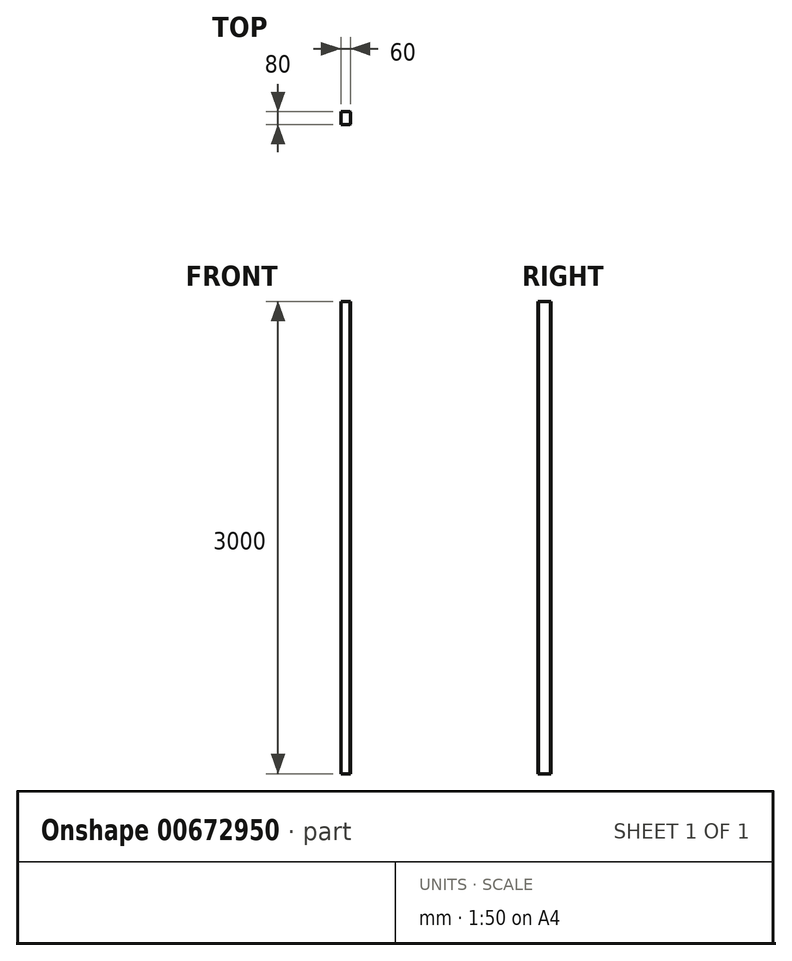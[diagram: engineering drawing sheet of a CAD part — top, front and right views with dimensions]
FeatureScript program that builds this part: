
annotation { "Feature Type Name" : "Feature", "Feature Type Description" : "" }
export const myFeature = defineFeature(function(context is Context, id is Id, definition is map)
    precondition{}
    {
        {
            var Q0;
            Q0=qCreatedBy(makeId("Top.planeOp"),FACE);
            var sketch = newSketch(context, id + "F0", { "sketchPlane" : qUnion([Q0])});
            skLineSegment(sketch, "E0.bottom", {"start": v(0, 0) * mm, "end": v(60, 0) * mm});
            skLineSegment(sketch, "E0.top", {"start": v(0, 80) * mm, "end": v(60, 80) * mm});
            skLineSegment(sketch, "E0.left", {"start": v(0, 0) * mm, "end": v(0, 80) * mm});
            skLineSegment(sketch, "E0.right", {"start": v(60, 0) * mm, "end": v(60, 80) * mm});
            skSolve(sketch);
        }
        {
            var Q0;
            Q0=makeQuery(id+"F0.imprint","IMPRINT",FACE,{"disambiguationData":[TD([[makeQuery(id+"F0.imprint","IMPRINT",EDGE,{"derivedFrom":sQuery(id+"F0.wireOp",EDGE,"E0.bottom")}),1.0]])]});
            extrude(context, id + "F1", {"entities" : qUnion([Q0]), "depth" : 3000 * mm, "offsetDistance" : 25 * mm});
        }
        {
            var Q0;
            Q0=makeQuery(id+"F1.opExtrude","SWEPT_EDGE",EDGE,{"disambiguationData":[OSD([sQuery(id+"F0.wireOp",EDGE,"E0.bottom"),sQuery(id+"F0.wireOp",EDGE,"E0.right")])]});
            chamfer(context, id + "F2", {"entities" : qUnion([Q0]), "width" : 1 * mm, "tangentPropagation" : true});
        }
        {
            var Q0;
            Q0=makeQuery(id+"F1.opExtrude","SWEPT_EDGE",EDGE,{"disambiguationData":[OSD([sQuery(id+"F0.wireOp",EDGE,"E0.bottom"),sQuery(id+"F0.wireOp",EDGE,"E0.left")])]});
            chamfer(context, id + "F3", {"entities" : qUnion([Q0]), "width" : 1 * mm, "tangentPropagation" : true});
        }
        {
            var Q0;
            Q0=makeQuery(id+"F1.opExtrude","SWEPT_EDGE",EDGE,{"disambiguationData":[OSD([sQuery(id+"F0.wireOp",EDGE,"E0.top"),sQuery(id+"F0.wireOp",EDGE,"E0.right")])]});
            chamfer(context, id + "F4", {"entities" : qUnion([Q0]), "width" : 1 * mm, "tangentPropagation" : true});
        }
        {
            var Q0;
            Q0=makeQuery(id+"F1.opExtrude","SWEPT_EDGE",EDGE,{"disambiguationData":[OSD([sQuery(id+"F0.wireOp",EDGE,"E0.top"),sQuery(id+"F0.wireOp",EDGE,"E0.left")])]});
            chamfer(context, id + "F5", {"entities" : qUnion([Q0]), "width" : 1 * mm, "tangentPropagation" : true});
        }
    });
